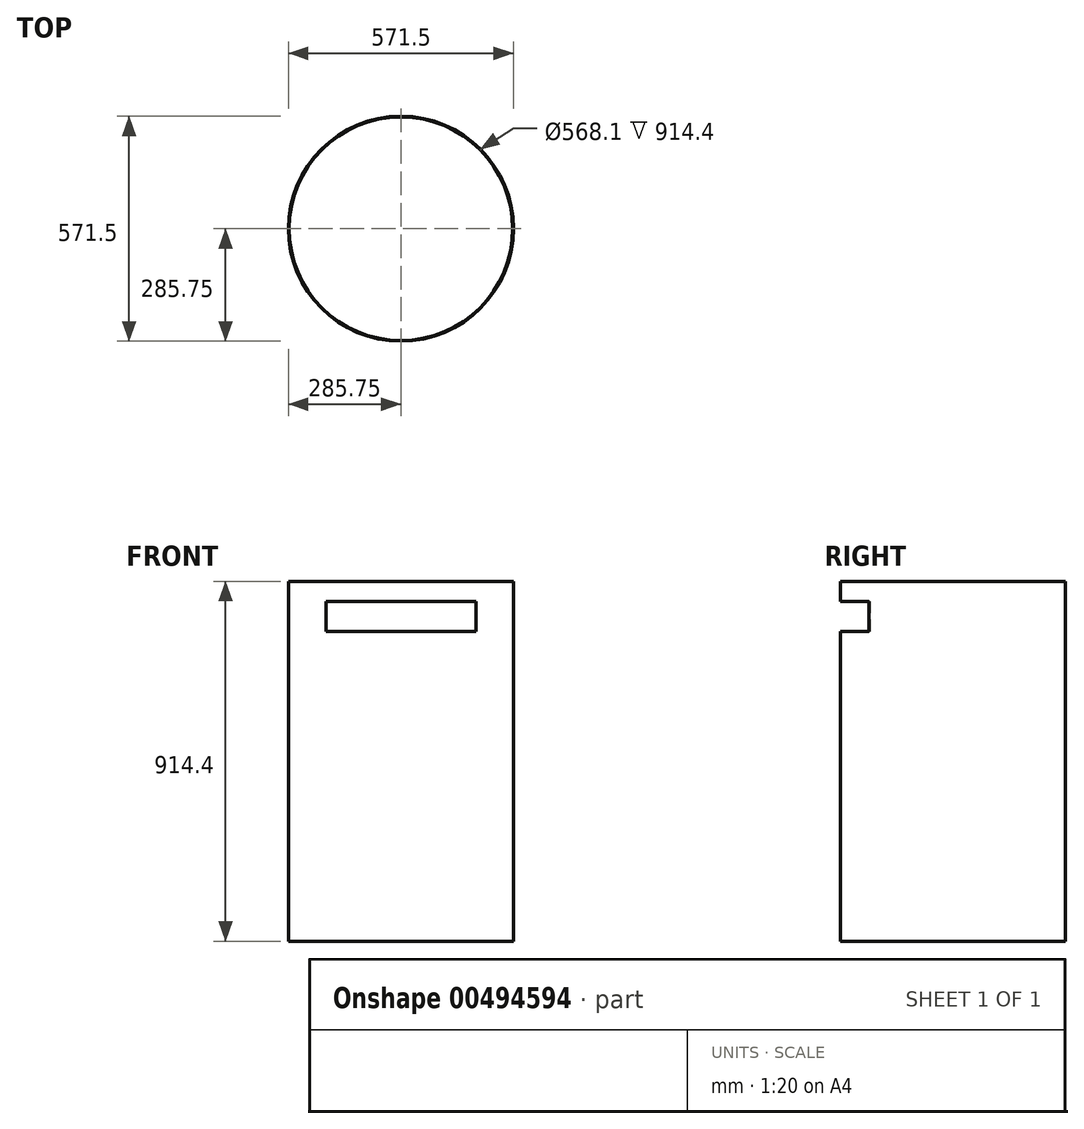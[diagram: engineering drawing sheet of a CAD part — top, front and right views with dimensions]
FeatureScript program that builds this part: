
annotation { "Feature Type Name" : "Feature", "Feature Type Description" : "" }
export const myFeature = defineFeature(function(context is Context, id is Id, definition is map)
    precondition{}
    {
        {
            var Q0;
            Q0=qCreatedBy(makeId("Top.planeOp"),FACE);
            var sketch = newSketch(context, id + "F0", { "sketchPlane" : qUnion([Q0])});
            skCircle(sketch, "E0", {"center": v(0, 0) * mm, "radius": 285.75 * mm});
            skCircle(sketch, "E1", {"center": v(0, 0) * mm, "radius": 284.05 * mm});
            skSolve(sketch);
        }
        {
            var Q0;
            Q0 = qSketchRegion(id + "F0", true);
            extrude(context, id + "F1", {"entities" : qUnion([Q0]), "depth" : 914.4 * mm});
        }
        {
            var Q0;
            Q0=qCreatedBy(makeId("Front.planeOp"),FACE);
            var sketch = newSketch(context, id + "F2", { "sketchPlane" : qUnion([Q0])});
            skLineSegment(sketch, "E2.bottom", {"start": v(-190.5, 863.6) * mm, "end": v(190.5, 863.6) * mm});
            skLineSegment(sketch, "E2.top", {"start": v(-190.5, 787.4) * mm, "end": v(190.5, 787.4) * mm});
            skLineSegment(sketch, "E2.left", {"start": v(-190.5, 863.6) * mm, "end": v(-190.5, 787.4) * mm});
            skLineSegment(sketch, "E2.right", {"start": v(190.5, 863.6) * mm, "end": v(190.5, 787.4) * mm});
            skSolve(sketch);
        }
        {
            var Q0;
            Q0 = qSketchRegion(id + "F2", true);
            extrude(context, id + "F3", {"entities" : qUnion([Q0]), "operationType" : NewBodyOperationType.REMOVE, "endBound" : BoundingType.THROUGH_ALL, "depth" : 25.4 * mm, "offsetDistance" : 25.4 * mm});
        }
    });
